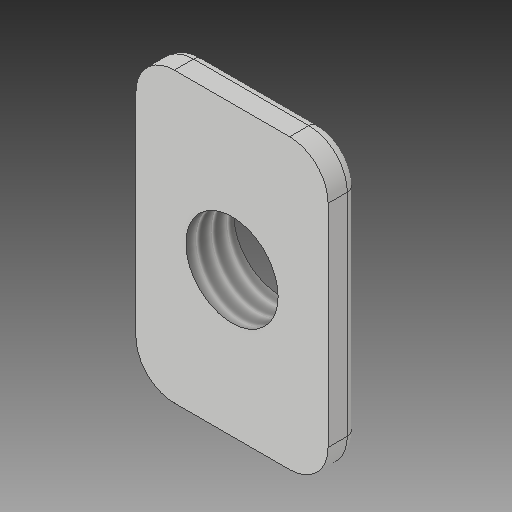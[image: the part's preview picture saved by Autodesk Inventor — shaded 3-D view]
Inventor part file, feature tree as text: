
AUTODESK INVENTOR PART (.ipt)
format: ipt  version: 2018 (Build 220112000, 112)  size: 158,720 bytes
history: native  units: mm
features: other x3, sketch x2
ambient origin geometry x8: Origin, YZ Plane, XZ Plane, XY Plane, X Axis, Y Axis, Z Axis, Center Point
bodies: Solid1 (feature_tree)
feature tree (5):
  other  "M5 Tee Nut-Generic.ipt"
  other  "Solid1::M5 Tee Nut-Generic.ipt"
  other  "TaggingFeature1"
  sketch  "Sketch1"  dims[d0=10.0mm]
  sketch  "Sketch2"
